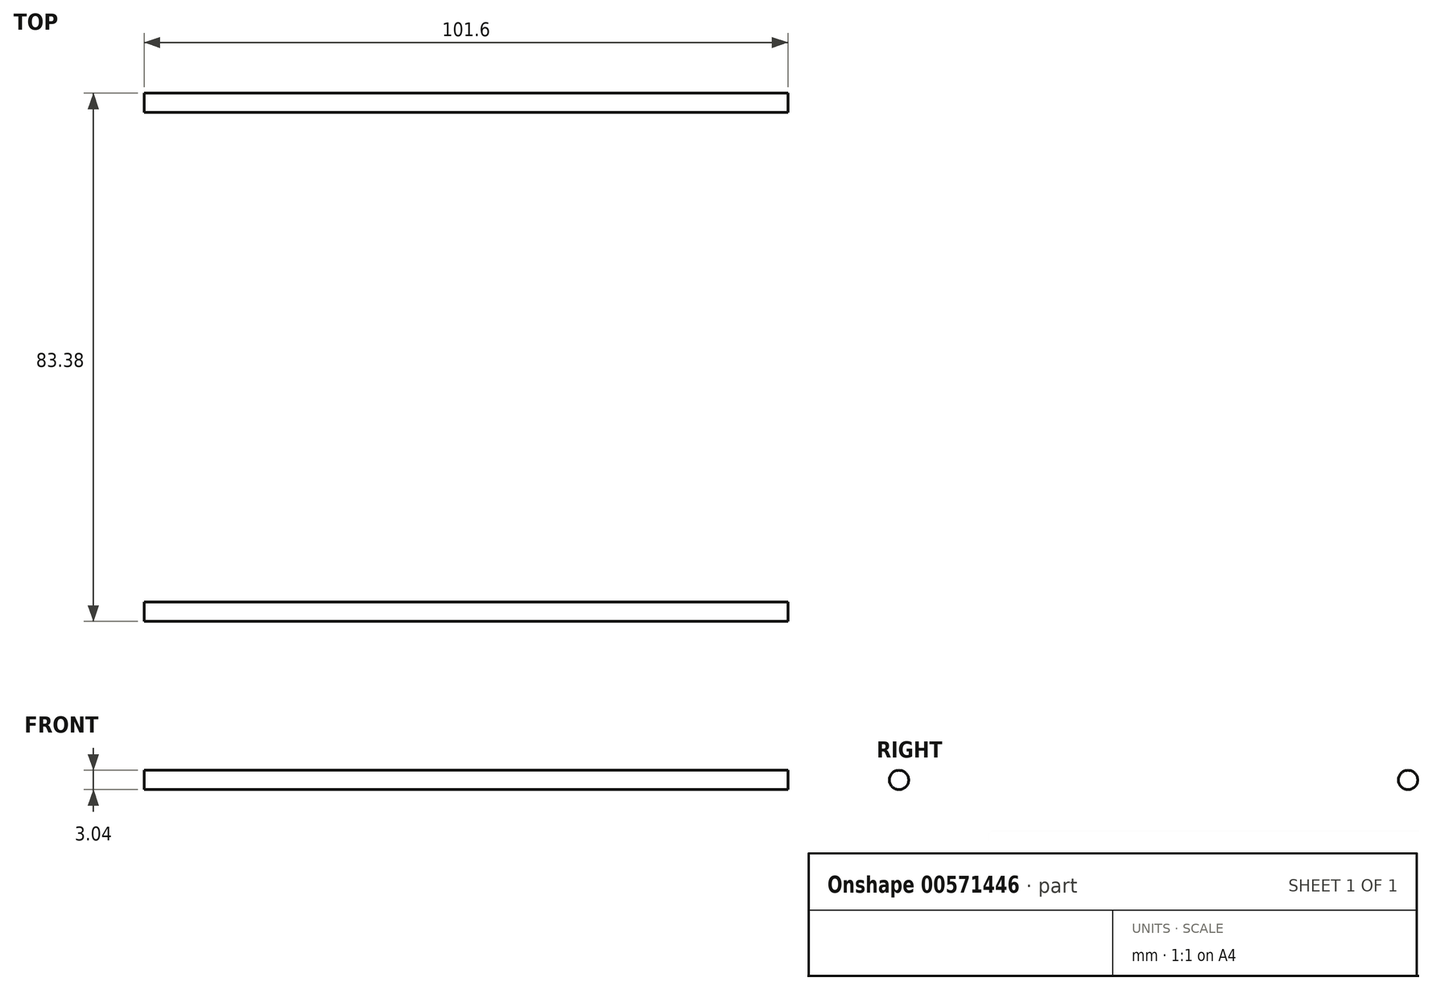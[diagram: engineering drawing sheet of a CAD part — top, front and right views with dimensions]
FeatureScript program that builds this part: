
annotation { "Feature Type Name" : "Feature", "Feature Type Description" : "" }
export const myFeature = defineFeature(function(context is Context, id is Id, definition is map)
    precondition{}
    {
        {
            var Q0;
            Q0=qCreatedBy(makeId("Right.planeOp"),FACE);
            var sketch = newSketch(context, id + "F0", { "sketchPlane" : qUnion([Q0])});
            skCircle(sketch, "E0", {"center": v(-44.03, 0) * mm, "radius": 1.52 * mm});
            skCircle(sketch, "E1", {"center": v(36.3, 0) * mm, "radius": 1.52 * mm});
            skSolve(sketch);
        }
        {
            var Q0;
            Q0 = qSketchRegion(id + "F0", true);
            extrude(context, id + "F1", {"entities" : qUnion([Q0]), "depth" : 101.6 * mm, "offsetDistance" : 25.4 * mm});
        }
    });
